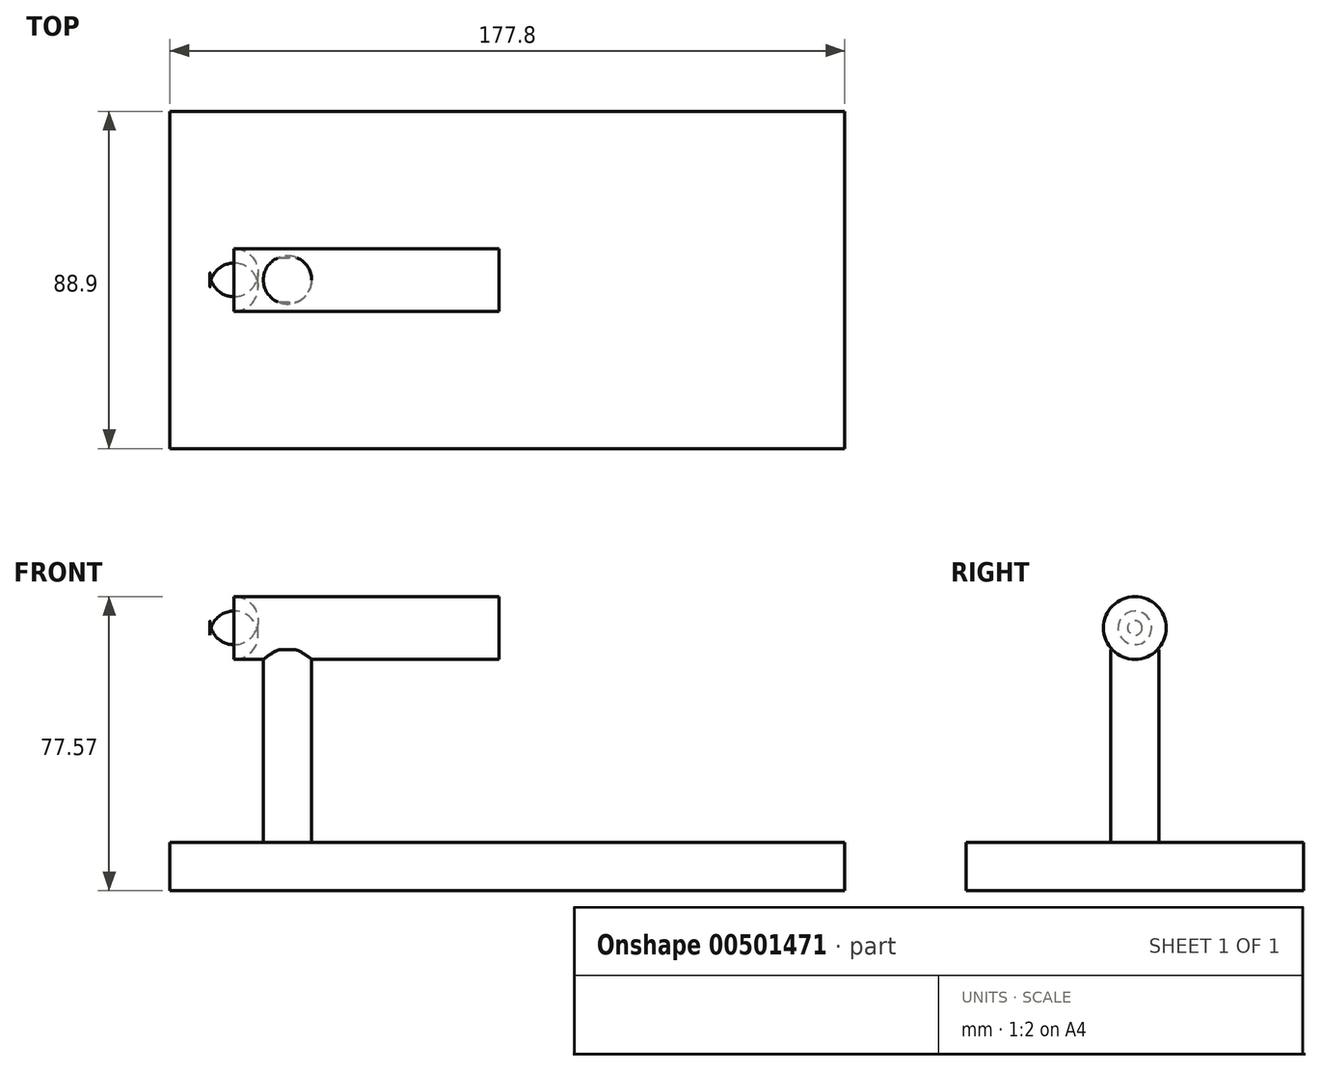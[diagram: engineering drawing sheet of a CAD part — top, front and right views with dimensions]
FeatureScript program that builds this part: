
annotation { "Feature Type Name" : "Feature", "Feature Type Description" : "" }
export const myFeature = defineFeature(function(context is Context, id is Id, definition is map)
    precondition{}
    {
        {
            var Q0;
            Q0=qCreatedBy(makeId("Front.planeOp"),FACE);
            var sketch = newSketch(context, id + "F0", { "sketchPlane" : qUnion([Q0])});
            skLineSegment(sketch, "E0.bottom", {"start": v(-86.73, -56.6) * mm, "end": v(91.07, -56.6) * mm});
            skLineSegment(sketch, "E0.top", {"start": v(-86.73, -69.3) * mm, "end": v(91.07, -69.3) * mm});
            skLineSegment(sketch, "E0.left", {"start": v(-86.73, -56.6) * mm, "end": v(-86.73, -69.3) * mm});
            skLineSegment(sketch, "E0.right", {"start": v(91.07, -56.6) * mm, "end": v(91.07, -69.3) * mm});
            skSolve(sketch);
        }
        {
            var Q0;
            Q0 = qSketchRegion(id + "F0", true);
            extrude(context, id + "F1", {"entities" : qUnion([Q0]), "endBound" : BoundingType.SYMMETRIC, "depth" : 88.9 * mm});
        }
        {
            var Q0;
            Q0=makeQuery(id+"F1.opExtrude","SWEPT_FACE",FACE,{"disambiguationData":[OSD([sQuery(id+"F0.wireOp",EDGE,"E0.bottom")])]});
            var sketch = newSketch(context, id + "F2", { "sketchPlane" : qUnion([Q0])});
            skCircle(sketch, "E1", {"center": v(-55.75, 0) * mm, "radius": 6.35 * mm});
            skSolve(sketch);
        }
        {
            var Q0;
            Q0=makeQuery(id+"F2.imprint","IMPRINT",FACE,{"disambiguationData":[TD([[makeQuery(id+"F2.imprint","IMPRINT",EDGE,{"derivedFrom":sQuery(id+"F2.wireOp",EDGE,"E1")}),1.0]])]});
            extrude(context, id + "F3", {"entities" : qUnion([Q0]), "operationType" : NewBodyOperationType.ADD, "depth" : 50.8 * mm});
        }
        {
            var Q0;
            Q0=qCreatedBy(makeId("Right.planeOp"),FACE);
            var sketch = newSketch(context, id + "F4", { "sketchPlane" : qUnion([Q0])});
            skCircle(sketch, "E2", {"center": v(0, 3.14) * mm, "radius": 10.73 * mm});
            skSolve(sketch);
        }
        {
            var Q0;
            Q0 = qSketchRegion(id + "F4", true);
            extrude(context, id + "F5", {"entities" : qUnion([Q0]), "operationType" : NewBodyOperationType.REMOVE, "oppositeDirection" : true, "depth" : 127 * mm});
        }
        {
            var Q0;
            Q0=qCreatedBy(makeId("Right.planeOp"),FACE);
            var sketch = newSketch(context, id + "F6", { "sketchPlane" : qUnion([Q0])});
            skCircle(sketch, "E3", {"center": v(0, 0) * mm, "radius": 8.27 * mm});
            skSolve(sketch);
        }
        {
            var Q0;
            Q0=makeQuery(id+"F6.imprint","IMPRINT",FACE,{"disambiguationData":[TD([[makeQuery(id+"F6.imprint","IMPRINT",EDGE,{"derivedFrom":sQuery(id+"F6.wireOp",EDGE,"E3")}),1.0]])]});
            extrude(context, id + "F7", {"entities" : qUnion([Q0]), "operationType" : NewBodyOperationType.ADD, "depth" : -76.2 * mm});
        }
        {
            var Q0;
            Q0=makeQuery(id+"F7.opExtrude","CAP_EDGE",EDGE,{"disambiguationData":[OSD([sQuery(id+"F6.wireOp",EDGE,"E3")])],"isStart":false});
            fillet(context, id + "F8", {"entities" : qUnion([Q0]), "radius" : 6.35 * mm, "tangentPropagation" : true, "allowEdgeOverflow" : false});
        }
    });
